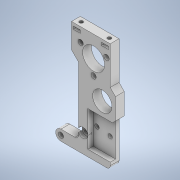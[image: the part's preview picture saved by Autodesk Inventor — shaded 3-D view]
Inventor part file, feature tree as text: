
AUTODESK INVENTOR PART (.ipt)
format: ipt  version: 2020.2 (Build 242310000, 310)  size: 283,648 bytes
history: native  units: mm
features: extrude x6, sketch x6, fillet x2, thread x2, projected_geometry x2
ambient origin geometry x8: Origin, YZ Plane, XZ Plane, XY Plane, X Axis, Y Axis, Z Axis, Center Point
bodies: Solid1 (feature_tree)
feature tree (18):
  extrude  "Extrusion1"  Depth=6.0mm
  fillet  "Fillet1"  Radius=28.0mm
  fillet  "Fillet2"  Radius=6.0mm
  extrude  "Extrusion2"  Depth=3.0mm
  extrude  "Extrusion3"  Depth=56.0mm
  thread  "Thread1"  [1 undecoded]
  thread  "Thread2"  [1 undecoded]
  extrude  "Extrusion4"  Depth=12.5mm
  extrude  "Extrusion5"  Depth=1.6mm
  extrude  "Extrusion6"  Depth=10.0mm TaperAngle=360.0deg
  sketch  "Sketch1"  dims[d0=3.0mm d1=6.0mm d2=28.0mm d3=6.0mm]
  sketch  "Sketch2"  dims[d4=0.0mm d5=3.0mm]
  sketch  "Sketch3"  dims[d6=18.0mm d7=56.0mm d8=11.0mm d9=4.5mm]
  projected_geometry  "Projected Loop1"
  sketch  "Sketch5"  dims[d10=25.5mm d11=12.5mm]
  sketch  "Sketch7"  dims[d12=19.15mm d14=1.6mm]
  sketch  "Sketch8"  dims[d17=12.0mm d18=30.0mm d20=360.0deg d22=4.0mm d23=14.0mm d24=45.0deg d25=3.0mm d26=12.0mm d27=6.0mm d28=135.0deg d29=135.0deg d30=5.0mm d31=0.0mm d32=3.0mm d33=10.5mm d34=2.5mm d35=2.5mm d36=14.5mm d37=7.5mm d38=2.5mm d39=15.0mm d40=13.5mm d41=2.0mm d42=2.0mm d43=12.75mm d44=20.0mm d45=23.75mm d46=3.0mm d47=0.0mm d48=2.0mm d49=2.0mm d50=2.5mm d51=2.5mm d52=3.0mm d53=3.0mm d54=6.0mm d55=0.0mm d56=7.0mm d57=0.0mm d58=7.0mm d59=0.0mm d60=8.5mm d61=270.0deg d62=3.0mm d63=3.0mm d64=3.0mm d65=3.0mm d66=0.0mm d67=5.5mm d68=2.0mm d69=0.0mm d70=4.0mm d71=1.6mm d72=4.0mm d73=1.6mm d74=1.0mm d75=2.5mm d76=2.5mm d77=1.0mm d78=10.0mm d79=0.0mm d80=0.5mm d81=0.872665mm d82=0.5mm d83=0.872665mm]
  projected_geometry  "Projected Loop2"
note: 2 required parameter values undecoded (feature->parameter linkage not recoverable at this tier; creation-order binding heuristic only, values carry confidence <= 0.55)
